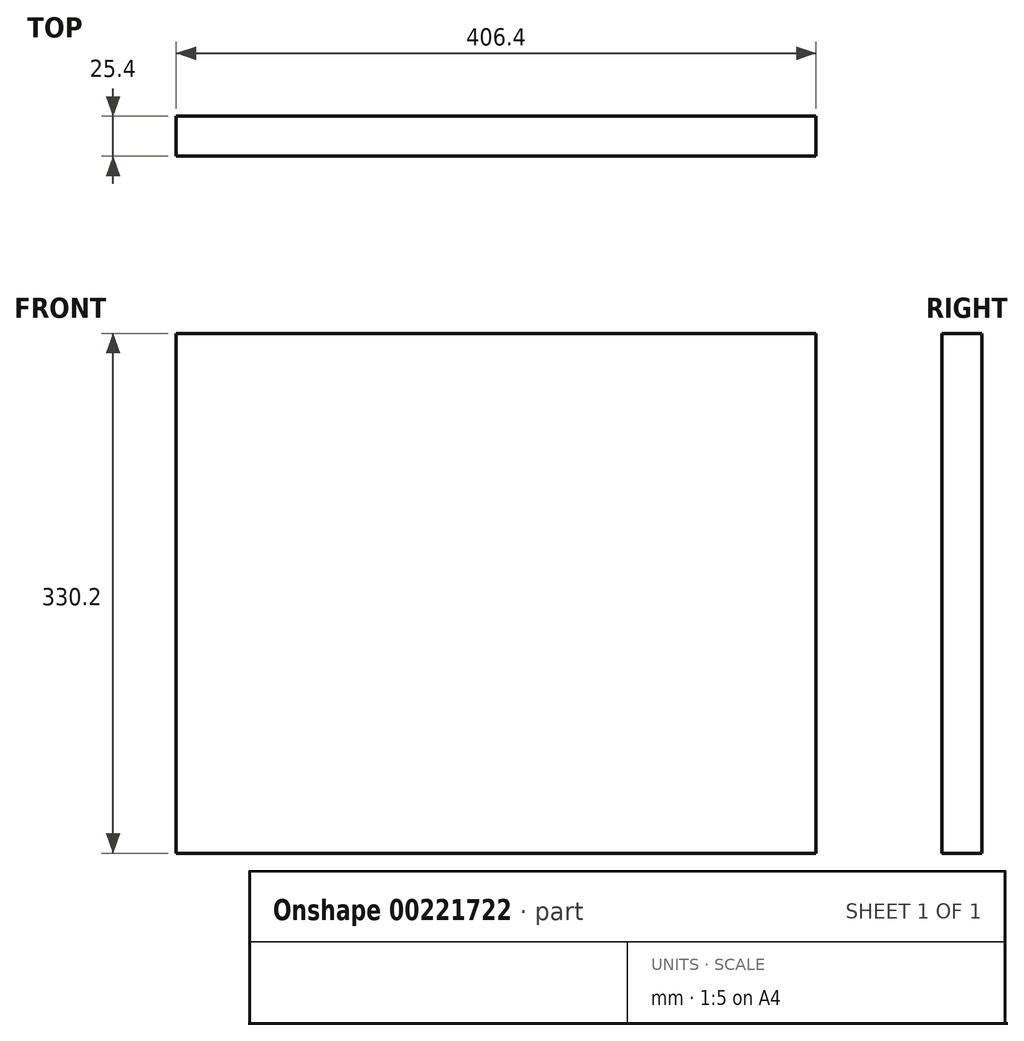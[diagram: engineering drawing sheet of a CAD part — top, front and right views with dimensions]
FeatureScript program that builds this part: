
annotation { "Feature Type Name" : "Feature", "Feature Type Description" : "" }
export const myFeature = defineFeature(function(context is Context, id is Id, definition is map)
    precondition{}
    {
        {
            var Q0;
            Q0=qCreatedBy(makeId("Front.planeOp"),FACE);
            var sketch = newSketch(context, id + "F0", { "sketchPlane" : qUnion([Q0])});
            skLineSegment(sketch, "E0.bottom", {"start": v(-91.78, 282.67) * mm, "end": v(314.62, 282.67) * mm});
            skLineSegment(sketch, "E0.top", {"start": v(-91.78, -47.53) * mm, "end": v(314.62, -47.53) * mm});
            skLineSegment(sketch, "E0.left", {"start": v(-91.78, 282.67) * mm, "end": v(-91.78, -47.53) * mm});
            skLineSegment(sketch, "E0.right", {"start": v(314.62, 282.67) * mm, "end": v(314.62, -47.53) * mm});
            skSolve(sketch);
        }
        {
            var Q0;
            Q0=makeQuery(id+"F0.imprint","IMPRINT",FACE,{"disambiguationData":[TD([[makeQuery(id+"F0.imprint","IMPRINT",EDGE,{"derivedFrom":sQuery(id+"F0.wireOp",EDGE,"E0.bottom")}),-1.0]])]});
            extrude(context, id + "F1", {"entities" : qUnion([Q0]), "depth" : 25.4 * mm});
        }
    });
